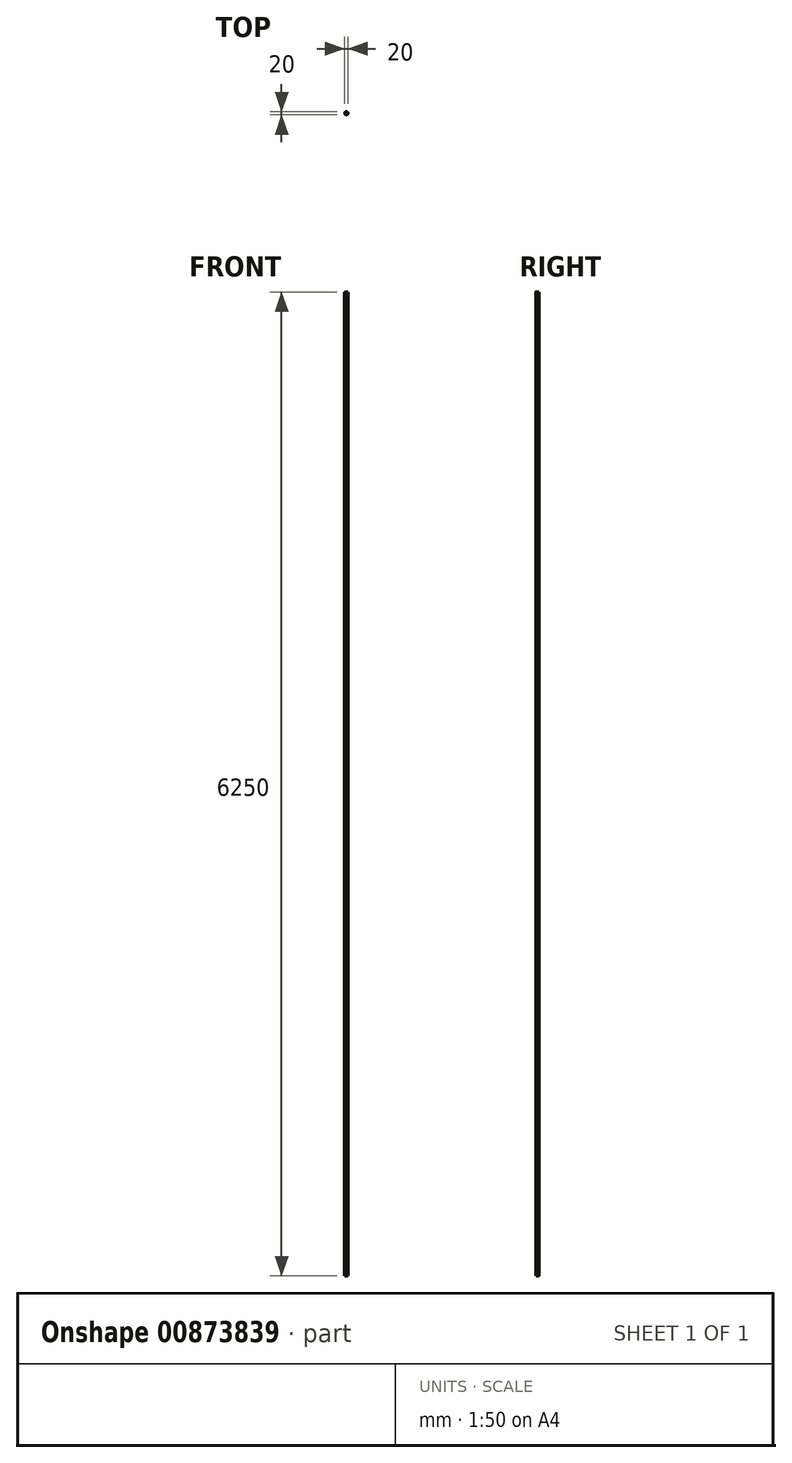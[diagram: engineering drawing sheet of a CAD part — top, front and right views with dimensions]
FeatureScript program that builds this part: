
annotation { "Feature Type Name" : "Feature", "Feature Type Description" : "" }
export const myFeature = defineFeature(function(context is Context, id is Id, definition is map)
    precondition{}
    {
        {
            var Q0;
            Q0=qCreatedBy(makeId("Top.planeOp"),FACE);
            var sketch = newSketch(context, id + "F0", { "sketchPlane" : qUnion([Q0])});
            skCircle(sketch, "E0", {"center": v(0, 0) * mm, "radius": 10 * mm});
            skSolve(sketch);
        }
        {
            var Q0;
            Q0 = qSketchRegion(id + "F0", true);
            extrude(context, id + "F1", {"entities" : qUnion([Q0]), "depth" : 6250 * mm, "offsetDistance" : 25 * mm});
        }
    });
